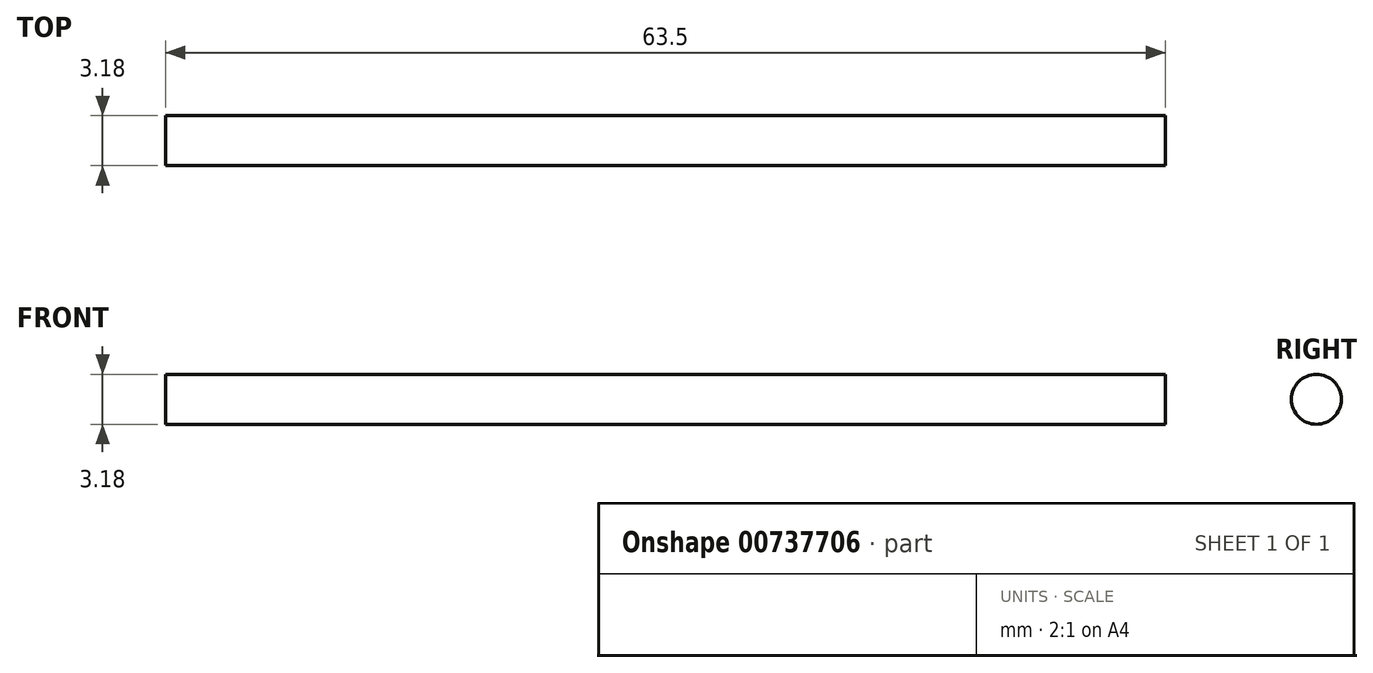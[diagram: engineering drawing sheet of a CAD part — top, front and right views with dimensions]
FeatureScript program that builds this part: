
annotation { "Feature Type Name" : "Feature", "Feature Type Description" : "" }
export const myFeature = defineFeature(function(context is Context, id is Id, definition is map)
    precondition{}
    {
        {
            var Q0;
            Q0=qCreatedBy(makeId("Right.planeOp"),FACE);
            var sketch = newSketch(context, id + "F0", { "sketchPlane" : qUnion([Q0])});
            skCircle(sketch, "E0", {"center": v(0, 0) * mm, "radius": 1.59 * mm});
            skSolve(sketch);
        }
        {
            var Q0;
            Q0=makeQuery(id+"F0.imprint","IMPRINT",FACE,{"disambiguationData":[TD([[makeQuery(id+"F0.imprint","IMPRINT",EDGE,{"derivedFrom":sQuery(id+"F0.wireOp",EDGE,"E0")}),1.0]])]});
            extrude(context, id + "F1", {"entities" : qUnion([Q0]), "depth" : 63.5 * mm, "offsetDistance" : 25.4 * mm});
        }
    });
